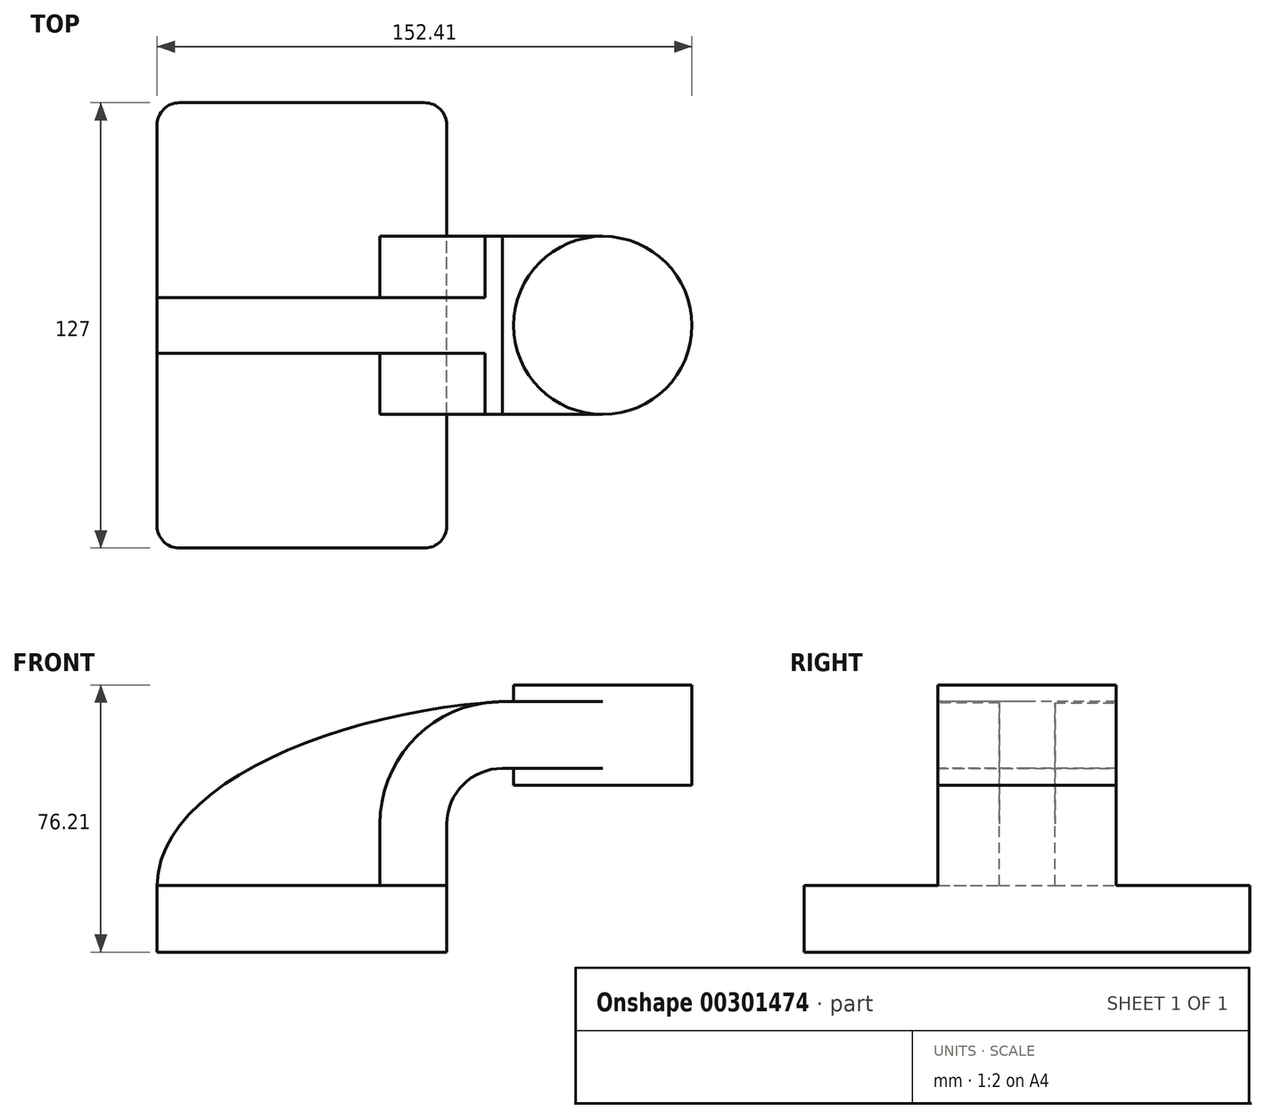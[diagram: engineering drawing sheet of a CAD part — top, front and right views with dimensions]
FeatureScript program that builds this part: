
annotation { "Feature Type Name" : "Feature", "Feature Type Description" : "" }
export const myFeature = defineFeature(function(context is Context, id is Id, definition is map)
    precondition{}
    {
        {
            var Q0;
            Q0=qCreatedBy(makeId("Front.planeOp"),FACE);
            var sketch = newSketch(context, id + "F0", { "sketchPlane" : qUnion([Q0])});
            skLineSegment(sketch, "E0.bottom", {"start": v(-41.28, 9.52) * mm, "end": v(41.27, 9.53) * mm});
            skLineSegment(sketch, "E0.top", {"start": v(-41.28, -9.53) * mm, "end": v(41.28, -9.53) * mm});
            skLineSegment(sketch, "E0.left", {"start": v(-41.28, 9.52) * mm, "end": v(-41.28, -9.53) * mm});
            skLineSegment(sketch, "E0.right", {"start": v(41.27, 9.53) * mm, "end": v(41.28, -9.52) * mm});
            skPoint(sketch, "E0.middle", {"position": v(0, 0) * mm});
            skLineSegment(sketch, "E1.bottom", {"start": v(60.32, 66.67) * mm, "end": v(111.12, 66.67) * mm});
            skLineSegment(sketch, "E1.top", {"start": v(60.32, 38.1) * mm, "end": v(111.12, 38.1) * mm});
            skLineSegment(sketch, "E1.left", {"start": v(60.32, 66.67) * mm, "end": v(60.32, 38.1) * mm});
            skLineSegment(sketch, "E1.right", {"start": v(111.12, 66.67) * mm, "end": v(111.12, 38.1) * mm});
            skPoint(sketch, "E1.middle", {"position": v(85.72, 52.39) * mm});
            skLineSegment(sketch, "E2", {"start": v(41.27, 9.53) * mm, "end": v(41.27, 27) * mm});
            skArc(sketch, "E3", {"start": v(41.27, 27) * mm, "mid": v(45.92, 38.23) * mm, "end": v(57.15, 42.88) * mm});
            skLineSegment(sketch, "E4", {"start": v(57.15, 42.88) * mm, "end": v(85.72, 42.88) * mm});
            skLineSegment(sketch, "E5.0", {"start": v(57.15, 61.93) * mm, "end": v(85.72, 61.93) * mm});
            skArc(sketch, "E5.1", {"start": v(22.22, 27) * mm, "mid": v(32.45, 51.7) * mm, "end": v(57.15, 61.93) * mm});
            skLineSegment(sketch, "E5.2", {"start": v(22.22, 9.53) * mm, "end": v(22.22, 27) * mm});
            skLineSegment(sketch, "E6", {"start": v(85.72, 38.1) * mm, "end": v(85.72, 66.67) * mm});
            skFitSpline(sketch, "E7", {"points": [v(-41.28, 9.52) * mm, v(57.15, 61.93) * mm], "startDerivative": vector(1.19, 87.56) * mm, "endDerivative": vector(138.95, 8.1) * mm});
            skSolve(sketch);
        }
        {
            var Q0;
            Q0=makeQuery(id+"F0.imprint","IMPRINT",FACE,{"disambiguationData":[TD([[makeQuery(id+"F0.imprint","IMPRINT",EDGE,{"derivedFrom":sQuery(id+"F0.wireOp",EDGE,"E0.top")}),1.0]])]});
            extrude(context, id + "F1", {"entities" : qUnion([Q0]), "endBound" : BoundingType.SYMMETRIC, "depth" : 127 * mm});
        }
        {
            var Q0;
            {var subQ1=sQuery(id+"F0.wireOp",EDGE,"E2");Q0=makeQuery(id+"F0.imprint","IMPRINT",FACE,{"disambiguationData":[TD([[makeQuery(id+"F0.imprint","IMPRINT",EDGE,{"derivedFrom":subQ1}),1.0]])]});}
            extrude(context, id + "F2", {"entities" : qUnion([Q0]), "operationType" : NewBodyOperationType.ADD, "endBound" : BoundingType.SYMMETRIC, "depth" : 50.8 * mm});
        }
        {
            var Q0;
            {var subQ3=sQuery(id+"F0.wireOp",EDGE,"E5.2");Q0=makeQuery(id+"F0.imprint","IMPRINT",FACE,{"disambiguationData":[TD([[makeQuery(id+"F0.imprint","IMPRINT",EDGE,{"derivedFrom":subQ3}),1.0]])]});}
            extrude(context, id + "F3", {"entities" : qUnion([Q0]), "operationType" : NewBodyOperationType.ADD, "endBound" : BoundingType.SYMMETRIC, "depth" : 15.88 * mm});
        }
        {
            var Q0;
            {var subQ0=sQuery(id+"F0.wireOp",EDGE,"E5.0");var subQ1=sQuery(id+"F0.wireOp",EDGE,"E1.left");var subQ2=makeQuery(id+"F0.imprint","INTERSECT",VERTEX,{"derivedFrom":[subQ1,subQ0]});Q0=makeQuery(id+"F0.imprint","IMPRINT",FACE,{"disambiguationData":[TD([[makeQuery(id+"F0.imprint","IMPRINT",EDGE,{"disambiguationData":[TD([[subQ2,-1.0]])],"derivedFrom":subQ1}),1.0]])]});}
            extrude(context, id + "F4", {"entities" : qUnion([Q0]), "operationType" : NewBodyOperationType.ADD, "endBound" : BoundingType.SYMMETRIC, "depth" : 50.8 * mm});
        }
        {
            var Q0;
            {var subQ4=sQuery(id+"F0.wireOp",EDGE,"E1.right");Q0=makeQuery(id+"F0.imprint","IMPRINT",FACE,{"disambiguationData":[TD([[makeQuery(id+"F0.imprint","IMPRINT",EDGE,{"derivedFrom":subQ4}),-1.0]])]});}
            var Q1;
            Q1=sQuery(id+"F0.wireOp",EDGE,"E6");
            revolve(context, id + "F5", {"operationType" : NewBodyOperationType.ADD, "entities" : qUnion([Q0]), "axis" : qUnion([Q1]), "revolveType" : RevolveType.FULL});
        }
        {
            var Q0;
            Q0=makeQuery(id+"F1.opExtrude","CAP_EDGE",EDGE,{"disambiguationData":[OSD([sQuery(id+"F0.wireOp",EDGE,"E0.left")])],"isStart":false});
            var Q1;
            Q1=makeQuery(id+"F1.opExtrude","CAP_EDGE",EDGE,{"disambiguationData":[OSD([sQuery(id+"F0.wireOp",EDGE,"E0.right")])],"isStart":false});
            var Q2;
            Q2=makeQuery(id+"F1.opExtrude","CAP_EDGE",EDGE,{"disambiguationData":[OSD([sQuery(id+"F0.wireOp",EDGE,"E0.right")])],"isStart":true});
            var Q3;
            Q3=makeQuery(id+"F1.opExtrude","CAP_EDGE",EDGE,{"disambiguationData":[OSD([sQuery(id+"F0.wireOp",EDGE,"E0.left")])],"isStart":true});
            fillet(context, id + "F6", {"entities" : qUnion([Q0, Q1, Q2, Q3]), "radius" : 6.35 * mm, "tangentPropagation" : true, "allowEdgeOverflow" : false});
        }
    });
